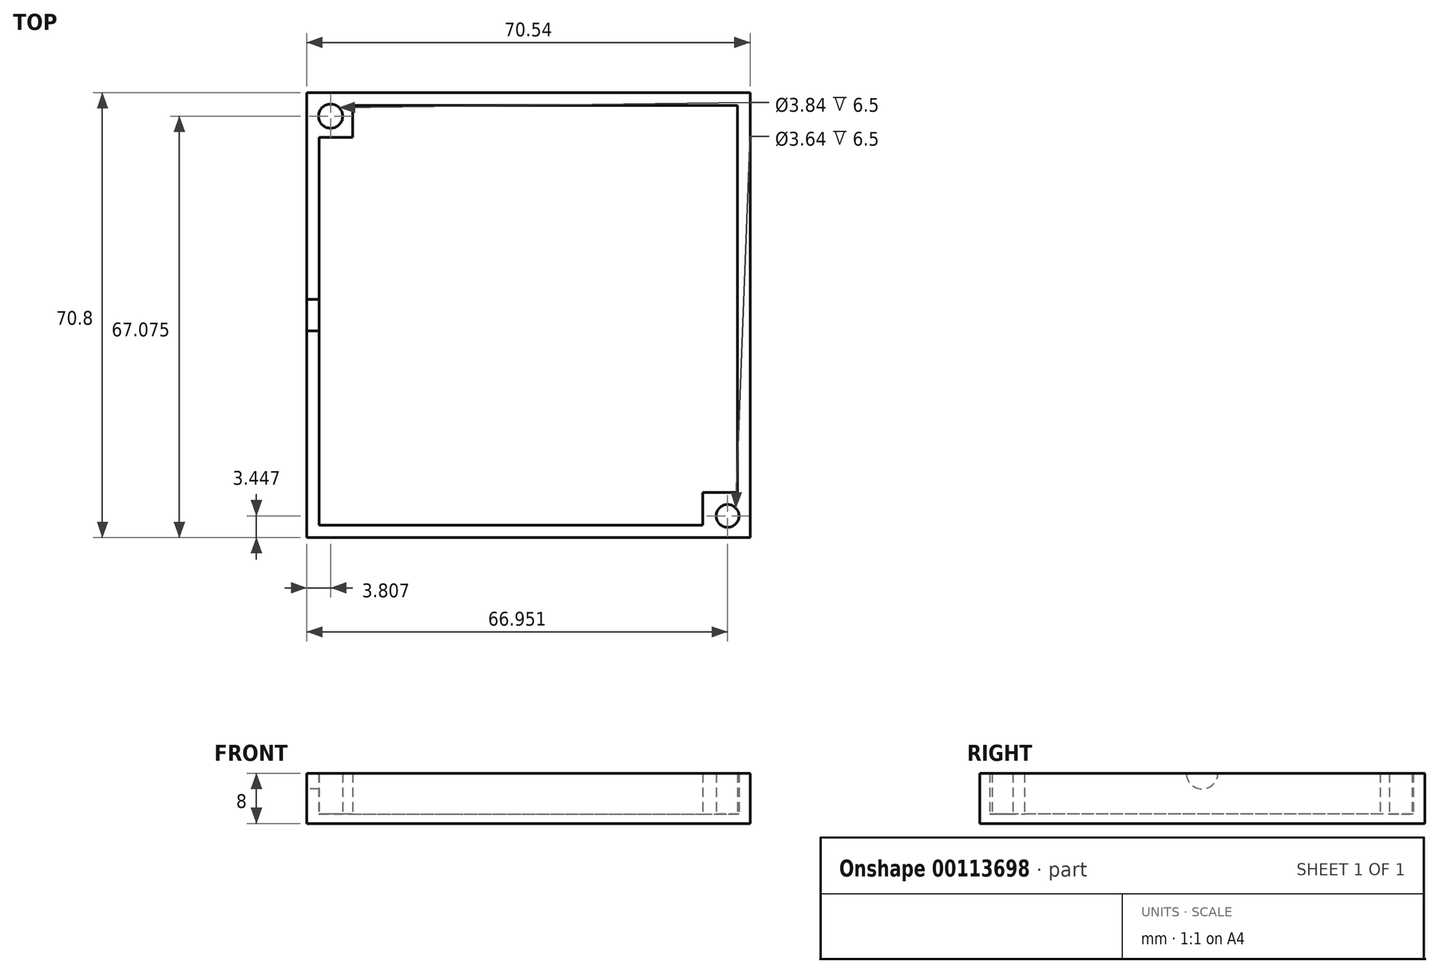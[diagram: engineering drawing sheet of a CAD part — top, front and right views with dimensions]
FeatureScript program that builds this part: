
annotation { "Feature Type Name" : "Feature", "Feature Type Description" : "" }
export const myFeature = defineFeature(function(context is Context, id is Id, definition is map)
    precondition{}
    {
        {
            var Q0;
            Q0=qCreatedBy(makeId("Top.planeOp"),FACE);
            var sketch = newSketch(context, id + "F0", { "sketchPlane" : qUnion([Q0])});
            skLineSegment(sketch, "E0.bottom", {"start": v(35.27, -35.4) * mm, "end": v(-35.27, -35.4) * mm});
            skLineSegment(sketch, "E0.top", {"start": v(35.27, 35.4) * mm, "end": v(-35.27, 35.4) * mm});
            skLineSegment(sketch, "E0.left", {"start": v(35.27, -35.4) * mm, "end": v(35.27, 35.4) * mm});
            skLineSegment(sketch, "E0.right", {"start": v(-35.27, -35.4) * mm, "end": v(-35.27, 35.4) * mm});
            skPoint(sketch, "E0.middle", {"position": v(0, 0) * mm});
            skLineSegment(sketch, "E1.2", {"start": v(33.27, 33.4) * mm, "end": v(-27.99, 33.4) * mm});
            skLineSegment(sketch, "E1.3", {"start": v(-33.27, -33.4) * mm, "end": v(-33.27, 28.32) * mm});
            skPoint(sketch, "E2.first.point", {"position": v(-30.72, 33.4) * mm});
            skPoint(sketch, "E2.second.point", {"position": v(-33.27, 30.65) * mm});
            skPoint(sketch, "E2.third.point", {"position": v(-28.73, 28.76) * mm});
            skCircle(sketch, "E3", {"center": v(-31.46, 31.67) * mm, "radius": 1.92 * mm});
            skCircle(sketch, "E4", {"center": v(31.68, -31.95) * mm, "radius": 1.82 * mm});
            skLineSegment(sketch, "E5", {"start": v(-33.27, 28.32) * mm, "end": v(-27.99, 28.32) * mm});
            skLineSegment(sketch, "E6", {"start": v(-27.99, 28.32) * mm, "end": v(-27.99, 33.4) * mm});
            skLineSegment(sketch, "E7", {"start": v(33.27, -28.25) * mm, "end": v(27.75, -28.25) * mm});
            skLineSegment(sketch, "E8", {"start": v(27.75, -28.25) * mm, "end": v(27.75, -33.4) * mm});
            skLineSegment(sketch, "E9.trimOffspring", {"start": v(-30.62, 33.4) * mm, "end": v(-30.72, 33.4) * mm});
            skLineSegment(sketch, "E10.trimOffspring", {"start": v(33.27, -28.25) * mm, "end": v(33.27, 33.4) * mm});
            skLineSegment(sketch, "E11.trimOffspring", {"start": v(27.75, -33.4) * mm, "end": v(-33.27, -33.4) * mm});
            skSolve(sketch);
        }
        {
            var Q0;
            Q0=makeQuery(id+"F0.imprint","IMPRINT",FACE,{"disambiguationData":[TD([[makeQuery(id+"F0.imprint","IMPRINT",EDGE,{"derivedFrom":sQuery(id+"F0.wireOp",EDGE,"E1.0")}),-1.0]])]});
            var Q1;
            Q1=makeQuery(id+"F0.imprint","IMPRINT",FACE,{"disambiguationData":[TD([[makeQuery(id+"F0.imprint","IMPRINT",EDGE,{"derivedFrom":sQuery(id+"F0.wireOp",EDGE,"E0.bottom")}),-1.0]])]});
            var Q2;
            {var subQ0=sQuery(id+"F0.wireOp",EDGE,"E1.3");var subQ1=sQuery(id+"F0.wireOp",EDGE,"E1.0");var subQ2=makeQuery(id+"F0.imprint","INTERSECT",VERTEX,{"derivedFrom":[subQ1,subQ0]});Q2=makeQuery(id+"F0.imprint","IMPRINT",FACE,{"disambiguationData":[TD([[makeQuery(id+"F0.imprint","IMPRINT",EDGE,{"disambiguationData":[TD([[subQ2,1.0]])],"derivedFrom":subQ1}),-1.0]])]});}
            var Q3;
            {var subQ0=sQuery(id+"F0.wireOp",EDGE,"E1.3");var subQ1=sQuery(id+"F0.wireOp",EDGE,"E1.2");var subQ2=makeQuery(id+"F0.imprint","INTERSECT",VERTEX,{"derivedFrom":[subQ1,subQ0]});Q3=makeQuery(id+"F0.imprint","IMPRINT",FACE,{"disambiguationData":[TD([[makeQuery(id+"F0.imprint","IMPRINT",EDGE,{"disambiguationData":[TD([[subQ2,1.0]])],"derivedFrom":subQ1}),1.0]])]});}
            var Q4;
            Q4=makeQuery(id+"F0.imprint","IMPRINT",FACE,{"disambiguationData":[TD([[makeQuery(id+"F0.imprint","IMPRINT",EDGE,{"derivedFrom":sQuery(id+"F0.wireOp",EDGE,"E3")}),1.0]])]});
            var Q5;
            Q5=makeQuery(id+"F0.imprint","IMPRINT",FACE,{"disambiguationData":[TD([[makeQuery(id+"F0.imprint","IMPRINT",EDGE,{"derivedFrom":sQuery(id+"F0.wireOp",EDGE,"E4")}),1.0]])]});
            extrude(context, id + "F1", {"entities" : qUnion([Q0, Q1, Q2, Q3, Q4, Q5]), "depth" : 1.5 * mm});
        }
        {
            var Q0;
            Q0=makeQuery(id+"F0.imprint","IMPRINT",FACE,{"disambiguationData":[TD([[makeQuery(id+"F0.imprint","IMPRINT",EDGE,{"derivedFrom":sQuery(id+"F0.wireOp",EDGE,"E0.bottom")}),-1.0]])]});
            var Q1;
            Q1=makeQuery(id+"F0.imprint","IMPRINT",FACE,{"disambiguationData":[TD([[makeQuery(id+"F0.imprint","IMPRINT",EDGE,{"derivedFrom":sQuery(id+"F0.wireOp",EDGE,"E3")}),-1.0]])]});
            var Q2;
            Q2=makeQuery(id+"F0.imprint","IMPRINT",FACE,{"disambiguationData":[TD([[makeQuery(id+"F0.imprint","IMPRINT",EDGE,{"derivedFrom":sQuery(id+"F0.wireOp",EDGE,"E4")}),-1.0]])]});
            extrude(context, id + "F2", {"entities" : qUnion([Q0, Q1, Q2]), "operationType" : NewBodyOperationType.ADD, "depth" : 8 * mm});
        }
        {
            var Q0;
            {var subQ0=sQuery(id+"F0.wireOp",EDGE,"E0.right");Q0=makeQuery(id+"F2.boolean.opBoolean","MERGE",FACE,{"derivedFrom":[makeQuery(id+"F1.opExtrude","SWEPT_FACE",FACE,{"disambiguationData":[OSD([subQ0])]}),makeQuery(id+"F2.opExtrude","SWEPT_FACE",FACE,{"disambiguationData":[OSD([subQ0])]})]});}
            var sketch = newSketch(context, id + "F3", { "sketchPlane" : qUnion([Q0])});
            skPoint(sketch, "E12", {"position": v(0, 8) * mm});
            skSolve(sketch);
        }
        {
            var Q0;
            Q0=sQuery(id+"F3.wireOp",VERTEX,"E12");
            var Q1;
            Q1=makeQuery(id+"F1.opExtrude","SWEPT_BODY",BODY,{"disambiguationData":[OSD([sQuery(id+"F0.wireOp",EDGE,"E0.bottom"),sQuery(id+"F0.wireOp",EDGE,"E0.top"),sQuery(id+"F0.wireOp",EDGE,"E0.left"),sQuery(id+"F0.wireOp",EDGE,"E0.right")])]});
            var Q2;
            Q2=makeQuery(id+"F2.opExtrude","SWEPT_BODY",BODY,{"disambiguationData":[OSD([sQuery(id+"F0.wireOp",EDGE,"E0.bottom"),sQuery(id+"F0.wireOp",EDGE,"E0.top"),sQuery(id+"F0.wireOp",EDGE,"E0.left"),sQuery(id+"F0.wireOp",EDGE,"E0.right"),sQuery(id+"F0.wireOp",EDGE,"E1.0"),sQuery(id+"F0.wireOp",EDGE,"E1.1"),sQuery(id+"F0.wireOp",EDGE,"E1.2"),sQuery(id+"F0.wireOp",EDGE,"E1.3"),sQuery(id+"F0.wireOp",EDGE,"E2"),sQuery(id+"F0.wireOp",EDGE,"ce93bfd4-b4bf-4fb8-b677-0a82221e00d5")])]});
            hole(context, id + "F4", {"style" : HoleStyle.SIMPLE, "endStyle" : HoleEndStyle.BLIND, "holeDiameter" : 5 * mm, "holeDepth" : 10 * mm, "locations" : qUnion([Q0]), "scope" : qUnion([Q1, Q2])});
        }
    });
